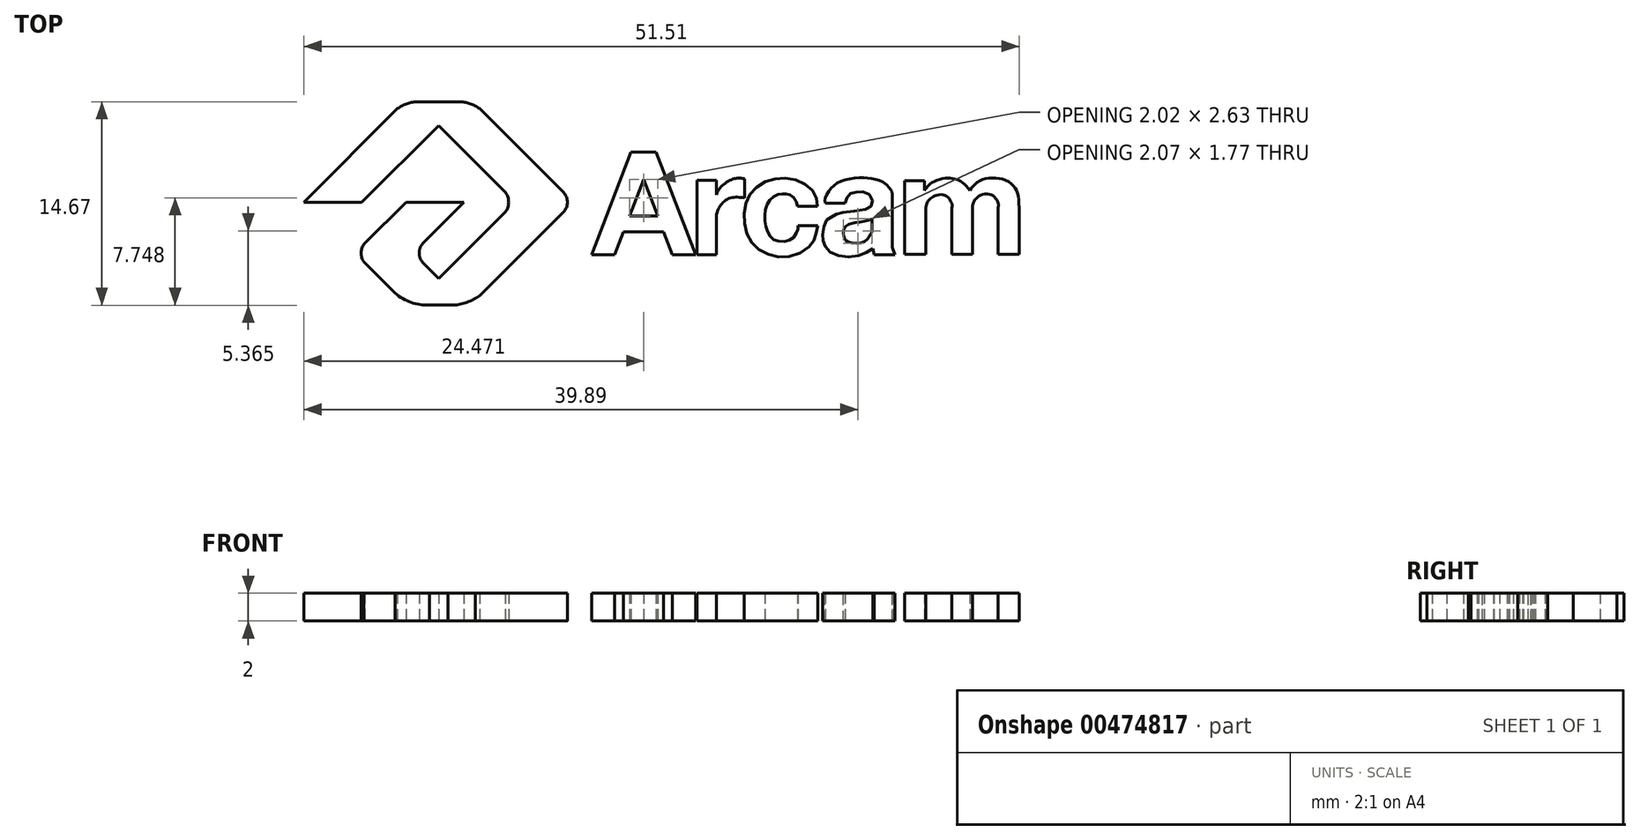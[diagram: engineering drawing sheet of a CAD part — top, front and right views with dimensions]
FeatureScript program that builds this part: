
annotation { "Feature Type Name" : "Feature", "Feature Type Description" : "" }
export const myFeature = defineFeature(function(context is Context, id is Id, definition is map)
    precondition{}
    {
        {
            var Q0;
            Q0=qCreatedBy(makeId("Top.planeOp"),FACE);
            var sketch = newSketch(context, id + "F0", { "sketchPlane" : qUnion([Q0])});
            skLineSegment(sketch, "E0", {"start": v(-75.28, 31.1) * mm, "end": v(-71.11, 31.1) * mm});
            skLineSegment(sketch, "E1", {"start": v(-71.11, 31.1) * mm, "end": v(-65.58, 36.63) * mm});
            skLineSegment(sketch, "E2", {"start": v(-65.58, 36.63) * mm, "end": v(-60.76, 31.8) * mm});
            skLineSegment(sketch, "E3", {"start": v(-60.76, 30.4) * mm, "end": v(-65.57, 25.58) * mm});
            skLineSegment(sketch, "E4", {"start": v(-65.57, 25.58) * mm, "end": v(-66.66, 26.67) * mm});
            skLineSegment(sketch, "E5", {"start": v(-66.66, 28.2) * mm, "end": v(-63.77, 31.1) * mm});
            skLineSegment(sketch, "E6", {"start": v(-63.77, 31.1) * mm, "end": v(-67.94, 31.1) * mm});
            skLineSegment(sketch, "E7", {"start": v(-67.94, 31.1) * mm, "end": v(-70.9, 28.13) * mm});
            skLineSegment(sketch, "E8", {"start": v(-70.95, 26.8) * mm, "end": v(-68.71, 24.55) * mm});
            skLineSegment(sketch, "E9", {"start": v(-62.55, 24.43) * mm, "end": v(-56.6, 30.4) * mm});
            skLineSegment(sketch, "E10", {"start": v(-56.6, 31.8) * mm, "end": v(-62.63, 37.84) * mm});
            skLineSegment(sketch, "E11", {"start": v(-68.54, 37.84) * mm, "end": v(-75.28, 31.1) * mm});
            skLineSegment(sketch, "E12", {"start": v(-67.04, 38.34) * mm, "end": v(-64.13, 38.34) * mm});
            skLineSegment(sketch, "E13", {"start": v(-66.55, 23.68) * mm, "end": v(-64.55, 23.68) * mm});
            skArc(sketch, "E14", {"start": v(-70.9, 28.13) * mm, "mid": v(-71.16, 27.47) * mm, "end": v(-70.95, 26.8) * mm});
            skArc(sketch, "E15", {"start": v(-66.66, 28.2) * mm, "mid": v(-66.97, 27.44) * mm, "end": v(-66.66, 26.67) * mm});
            skLineSegment(sketch, "E16", {"start": v(-65.57, 25.58) * mm, "end": v(-64.42, 24.43) * mm});
            skArc(sketch, "E17", {"start": v(-64.42, 24.43) * mm, "mid": v(-63.49, 24.05) * mm, "end": v(-62.55, 24.43) * mm});
            skArc(sketch, "E18", {"start": v(-64.9, 23.68) * mm, "mid": v(-63.89, 23.78) * mm, "end": v(-62.95, 24.16) * mm});
            skArc(sketch, "E19", {"start": v(-68.71, 24.55) * mm, "mid": v(-67.56, 23.87) * mm, "end": v(-66.24, 23.68) * mm});
            skArc(sketch, "E20", {"start": v(-60.76, 30.4) * mm, "mid": v(-60.54, 31.1) * mm, "end": v(-60.76, 31.8) * mm});
            skPoint(sketch, "E21.orphan", {"position": v(-56.6, 31.8) * mm});
            skPoint(sketch, "E22.start.orphan", {"position": v(-56.6, 30.4) * mm});
            skArc(sketch, "E23", {"start": v(-56.6, 30.4) * mm, "mid": v(-56.3, 31.1) * mm, "end": v(-56.6, 31.8) * mm});
            skArc(sketch, "E24", {"start": v(-62.63, 37.84) * mm, "mid": v(-63.33, 38.2) * mm, "end": v(-64.13, 38.34) * mm});
            skArc(sketch, "E25", {"start": v(-67.04, 38.34) * mm, "mid": v(-67.83, 38.2) * mm, "end": v(-68.54, 37.84) * mm});
            skLineSegment(sketch, "E26", {"start": v(-54.55, 27.3) * mm, "end": v(-51.71, 34.7) * mm});
            skLineSegment(sketch, "E27", {"start": v(-51.71, 34.7) * mm, "end": v(-49.9, 34.7) * mm});
            skLineSegment(sketch, "E28", {"start": v(-49.9, 34.7) * mm, "end": v(-47.07, 27.3) * mm});
            skLineSegment(sketch, "E29", {"start": v(-47.07, 27.3) * mm, "end": v(-48.73, 27.3) * mm});
            skLineSegment(sketch, "E30", {"start": v(-48.73, 27.3) * mm, "end": v(-49.36, 28.97) * mm});
            skLineSegment(sketch, "E31", {"start": v(-49.36, 28.97) * mm, "end": v(-52.25, 28.97) * mm});
            skLineSegment(sketch, "E32", {"start": v(-52.25, 28.97) * mm, "end": v(-52.9, 27.3) * mm});
            skLineSegment(sketch, "E33", {"start": v(-52.9, 27.3) * mm, "end": v(-54.55, 27.3) * mm});
            skLineSegment(sketch, "E34", {"start": v(-51.82, 30.1) * mm, "end": v(-50.8, 32.73) * mm});
            skLineSegment(sketch, "E35", {"start": v(-50.8, 32.73) * mm, "end": v(-49.8, 30.1) * mm});
            skLineSegment(sketch, "E36", {"start": v(-49.8, 30.1) * mm, "end": v(-51.82, 30.1) * mm});
            skLineSegment(sketch, "E37", {"start": v(-46.95, 27.3) * mm, "end": v(-46.95, 32.67) * mm});
            skLineSegment(sketch, "E38", {"start": v(-46.95, 32.67) * mm, "end": v(-45.58, 32.67) * mm});
            skLineSegment(sketch, "E39", {"start": v(-45.58, 32.67) * mm, "end": v(-45.58, 31.63) * mm});
            skLineSegment(sketch, "E40", {"start": v(-43.52, 32.78) * mm, "end": v(-43.52, 31.4) * mm});
            skLineSegment(sketch, "E41", {"start": v(-46.95, 27.3) * mm, "end": v(-45.58, 27.3) * mm});
            skLineSegment(sketch, "E42", {"start": v(-45.58, 27.3) * mm, "end": v(-45.58, 29.97) * mm});
            skFitSpline(sketch, "E43", {"points": [v(-45.58, 31.63) * mm, v(-45.38, 32.03) * mm, v(-44.85, 32.52) * mm, v(-44.28, 32.79) * mm, v(-43.86, 32.84) * mm, v(-43.52, 32.78) * mm], "startDerivative": vector(0.85, 2.06) * mm, "endDerivative": vector(2.01, -0.5) * mm});
            skFitSpline(sketch, "E44", {"points": [v(-43.52, 31.4) * mm, v(-44.29, 31.45) * mm, v(-44.99, 31.18) * mm, v(-45.46, 30.53) * mm, v(-45.58, 29.97) * mm], "startDerivative": vector(-2.98, 0.4) * mm, "endDerivative": vector(-0.32, -2.43) * mm});
            skLineSegment(sketch, "E45", {"start": v(-39.73, 30.81) * mm, "end": v(-38.29, 30.81) * mm});
            skLineSegment(sketch, "E46", {"start": v(-38.26, 29.4) * mm, "end": v(-39.68, 29.4) * mm});
            skFitSpline(sketch, "E47", {"points": [v(-38.29, 30.81) * mm, v(-38.48, 31.67) * mm, v(-39.34, 32.5) * mm, v(-40.73, 32.84) * mm, v(-42.05, 32.57) * mm, v(-43.09, 31.76) * mm, v(-43.54, 30.6) * mm, v(-43.48, 29.16) * mm, v(-42.88, 27.99) * mm, v(-41.62, 27.27) * mm, v(-40.18, 27.22) * mm, v(-38.83, 27.94) * mm, v(-38.47, 28.59) * mm, v(-38.26, 29.4) * mm], "startDerivative": vector(-1.29, 13.4) * mm, "endDerivative": vector(3.13, 13.27) * mm});
            skFitSpline(sketch, "E48", {"points": [v(-39.68, 29.4) * mm, v(-39.74, 29.03) * mm, v(-40.12, 28.47) * mm, v(-40.87, 28.27) * mm, v(-41.57, 28.5) * mm, v(-41.98, 29.24) * mm, v(-42.08, 30.08) * mm, v(-41.93, 30.91) * mm, v(-41.44, 31.5) * mm, v(-40.87, 31.7) * mm, v(-40.48, 31.68) * mm, v(-39.99, 31.43) * mm, v(-39.73, 30.81) * mm], "startDerivative": vector(-0.32, -5.47) * mm, "endDerivative": vector(2.15, -8.36) * mm});
            skFitSpline(sketch, "E49", {"points": [v(-36.29, 31.03) * mm, v(-36.19, 31.41) * mm, v(-35.92, 31.71) * mm, v(-35.47, 31.83) * mm, v(-34.9, 31.84) * mm, v(-34.37, 31.41) * mm, v(-34.38, 30.9) * mm, v(-34.69, 30.61) * mm, v(-36.3, 30.38) * mm, v(-36.98, 30.2) * mm, v(-37.35, 29.98) * mm, v(-37.64, 29.77) * mm, v(-37.89, 29.05) * mm, v(-37.89, 28.45) * mm, v(-37.78, 27.99) * mm, v(-37.33, 27.48) * mm, v(-36.12, 27.15) * mm, v(-35, 27.36) * mm, v(-34.3, 27.76) * mm], "startDerivative": vector(1.58, 8.96) * mm, "endDerivative": vector(10.57, 7.04) * mm});
            skFitSpline(sketch, "E50", {"points": [v(-37.73, 31.03) * mm, v(-37.74, 31.33) * mm, v(-37.46, 31.92) * mm, v(-36.91, 32.44) * mm, v(-36.1, 32.76) * mm, v(-35.03, 32.86) * mm, v(-34.28, 32.78) * mm, v(-33.51, 32.51) * mm, v(-32.95, 31.88) * mm, v(-32.9, 31.45) * mm], "startDerivative": vector(-0.74, 3.8) * mm, "endDerivative": vector(0, -4.72) * mm});
            skFitSpline(sketch, "E51", {"points": [v(-34.35, 29.92) * mm, v(-34.55, 29.8) * mm, v(-35.44, 29.64) * mm, v(-36.08, 29.48) * mm, v(-36.4, 29.15) * mm, v(-36.43, 28.75) * mm, v(-36.31, 28.41) * mm, v(-36.03, 28.22) * mm, v(-35, 28.2) * mm, v(-34.62, 28.55) * mm, v(-34.35, 28.93) * mm], "startDerivative": vector(-2.22, -1.8) * mm, "endDerivative": vector(2.77, 4) * mm});
            skLineSegment(sketch, "E52", {"start": v(-37.73, 31.03) * mm, "end": v(-36.29, 31.03) * mm});
            skLineSegment(sketch, "E53", {"start": v(-34.35, 29.92) * mm, "end": v(-34.35, 28.93) * mm});
            skLineSegment(sketch, "E54", {"start": v(-34.3, 27.76) * mm, "end": v(-34.2, 27.32) * mm});
            skLineSegment(sketch, "E55", {"start": v(-34.2, 27.32) * mm, "end": v(-32.7, 27.32) * mm});
            skLineSegment(sketch, "E56", {"start": v(-32.7, 27.32) * mm, "end": v(-32.9, 27.86) * mm});
            skLineSegment(sketch, "E57", {"start": v(-32.9, 27.86) * mm, "end": v(-32.9, 31.45) * mm});
            skLineSegment(sketch, "E58", {"start": v(-30.5, 30.7) * mm, "end": v(-30.5, 27.33) * mm});
            skLineSegment(sketch, "E59", {"start": v(-30.5, 27.33) * mm, "end": v(-32, 27.33) * mm});
            skLineSegment(sketch, "E60", {"start": v(-32, 27.33) * mm, "end": v(-32, 32.65) * mm});
            skLineSegment(sketch, "E61", {"start": v(-32, 32.65) * mm, "end": v(-30.57, 32.65) * mm});
            skLineSegment(sketch, "E62", {"start": v(-30.57, 32.65) * mm, "end": v(-30.57, 31.96) * mm});
            skLineSegment(sketch, "E63", {"start": v(-28.6, 30.7) * mm, "end": v(-28.6, 27.33) * mm});
            skLineSegment(sketch, "E64", {"start": v(-28.6, 27.33) * mm, "end": v(-27.13, 27.33) * mm});
            skLineSegment(sketch, "E65", {"start": v(-27.13, 27.33) * mm, "end": v(-27.13, 30.7) * mm});
            skLineSegment(sketch, "E66", {"start": v(-25.27, 30.7) * mm, "end": v(-25.27, 27.33) * mm});
            skLineSegment(sketch, "E67", {"start": v(-25.27, 27.33) * mm, "end": v(-23.77, 27.33) * mm});
            skLineSegment(sketch, "E68", {"start": v(-23.77, 27.33) * mm, "end": v(-23.77, 30.7) * mm});
            skFitSpline(sketch, "E69", {"points": [v(-30.57, 31.96) * mm, v(-30.4, 32.18) * mm, v(-30.03, 32.5) * mm, v(-29.14, 32.82) * mm, v(-28.49, 32.78) * mm, v(-27.88, 32.54) * mm, v(-27.33, 31.96) * mm], "startDerivative": vector(1.45, 1.9) * mm, "endDerivative": vector(2.73, -3.47) * mm});
            skFitSpline(sketch, "E70", {"points": [v(-27.33, 31.96) * mm, v(-27.01, 32.33) * mm, v(-26.4, 32.73) * mm, v(-25.63, 32.85) * mm, v(-24.77, 32.7) * mm, v(-24.13, 32.23) * mm, v(-23.87, 31.71) * mm, v(-23.77, 30.7) * mm], "startDerivative": vector(2.43, 3.18) * mm, "endDerivative": vector(0.28, -6.58) * mm});
            skFitSpline(sketch, "E71", {"points": [v(-25.27, 30.7) * mm, v(-25.27, 31.04) * mm, v(-25.48, 31.39) * mm, v(-25.8, 31.64) * mm, v(-26.46, 31.63) * mm, v(-26.87, 31.35) * mm, v(-27.05, 31.08) * mm, v(-27.13, 30.7) * mm], "startDerivative": vector(0.34, 2.6) * mm, "endDerivative": vector(-0.36, -2.94) * mm});
            skFitSpline(sketch, "E72", {"points": [v(-28.6, 30.7) * mm, v(-28.6, 30.98) * mm, v(-28.82, 31.37) * mm, v(-29.14, 31.62) * mm, v(-29.71, 31.6) * mm, v(-30.1, 31.42) * mm, v(-30.36, 31.1) * mm, v(-30.5, 30.7) * mm], "startDerivative": vector(0.3, 2.27) * mm, "endDerivative": vector(-0.75, -2.85) * mm});
            skPoint(sketch, "E73.orphan", {"position": v(-65.58, 40.8) * mm});
            skPoint(sketch, "E74.orphan", {"position": v(-68.04, 38.34) * mm});
            skPoint(sketch, "E75.orphan", {"position": v(-63.13, 38.34) * mm});
            skPoint(sketch, "E76.orphan", {"position": v(-67.84, 23.68) * mm});
            skPoint(sketch, "E77.orphan", {"position": v(-63.3, 23.68) * mm});
            skPoint(sketch, "E78.orphan", {"position": v(-55.89, 31.1) * mm});
            skLineSegment(sketch, "E79", {"start": v(-65.58, 36.63) * mm, "end": v(-64.68, 37.53) * mm});
            skArc(sketch, "E80", {"start": v(-62.63, 37.84) * mm, "mid": v(-63.7, 38.02) * mm, "end": v(-64.68, 37.53) * mm});
            skSolve(sketch);
        }
        {
            var Q0;
            Q0 = qSketchRegion(id + "F0", true);
            extrude(context, id + "F1", {"entities" : qUnion([Q0]), "depth" : 2 * mm, "offsetDistance" : 25 * mm});
        }
    });
